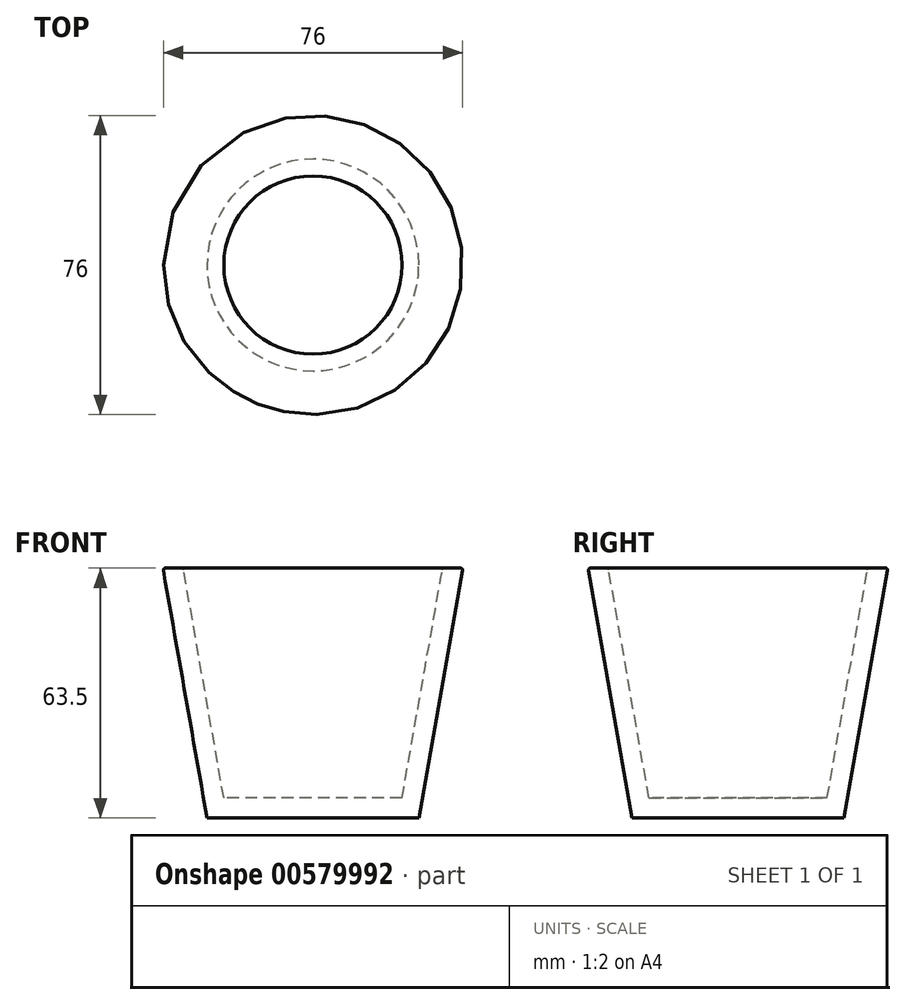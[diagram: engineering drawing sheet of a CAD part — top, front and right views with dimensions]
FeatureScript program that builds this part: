
annotation { "Feature Type Name" : "Feature", "Feature Type Description" : "" }
export const myFeature = defineFeature(function(context is Context, id is Id, definition is map)
    precondition{}
    {
        {
            var Q0;
            Q0=qCreatedBy(makeId("Front.planeOp"),FACE);
            var sketch = newSketch(context, id + "F0", { "sketchPlane" : qUnion([Q0])});
            skLineSegment(sketch, "E0", {"start": v(0, 63.5) * mm, "end": v(-38.1, 63.5) * mm});
            skLineSegment(sketch, "E1", {"start": v(-38.1, 63.5) * mm, "end": v(-26.9, 0) * mm});
            skLineSegment(sketch, "E2", {"start": v(-26.9, 0) * mm, "end": v(0, 0) * mm});
            skLineSegment(sketch, "E3", {"start": v(0, 0) * mm, "end": v(0, 63.5) * mm});
            skSolve(sketch);
        }
        {
            var Q0;
            Q0=makeQuery(id+"F0.imprint","IMPRINT",FACE,{"disambiguationData":[TD([[makeQuery(id+"F0.imprint","IMPRINT",EDGE,{"derivedFrom":sQuery(id+"F0.wireOp",EDGE,"E0")}),1.0]])]});
            var Q1;
            Q1=sQuery(id+"F0.wireOp",EDGE,"E3");
            revolve(context, id + "F1", {"entities" : qUnion([Q0]), "axis" : qUnion([Q1]), "revolveType" : RevolveType.FULL});
        }
        {
            var Q0;
            Q0=makeQuery(id+"F1.opRevolve","SWEPT_FACE",FACE,{"disambiguationData":[OSD([sQuery(id+"F0.wireOp",EDGE,"E0")])]});
            shell(context, id + "F2", {"entities" : qUnion([Q0]), "thickness" : 5.08 * mm});
        }
        {
            var Q0;
            Q0=makeQuery(id+"F1.opRevolve","SWEPT_EDGE",EDGE,{"disambiguationData":[OSD([sQuery(id+"F0.wireOp",EDGE,"E0"),sQuery(id+"F0.wireOp",EDGE,"E1")])]});
            var Q1;
            Q1=makeQuery(id+"F2.opShell","OFFSET_EDGE",EDGE,{"disambiguationData":[OSD([sQuery(id+"F0.wireOp",EDGE,"E0"),sQuery(id+"F0.wireOp",EDGE,"E1")])]});
            fillet(context, id + "F3", {"entities" : qUnion([Q0, Q1]), "radius" : 0.5 * mm, "tangentPropagation" : true, "allowEdgeOverflow" : false});
        }
    });
